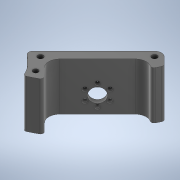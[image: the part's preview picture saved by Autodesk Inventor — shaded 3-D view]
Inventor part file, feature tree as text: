
AUTODESK INVENTOR PART (.ipt)
format: ipt  version: 2020 (Build 240168000, 168)  size: 688,128 bytes
history: native  units: mm
features: extrude x6, sketch x5, projected_geometry x2, other x1, chamfer x1, fillet x1
ambient origin geometry x8: Origin, YZ Plane, XZ Plane, XY Plane, X Axis, Y Axis, Z Axis, Center Point
bodies: Body1 (feature_tree)
feature tree (16):
  other  "Твердое тело1"
  sketch  "Эскиз1"
  extrude  "Выдавливание10"  Depth=4.0mm
  sketch  "Эскиз6"
  extrude  "Выдавливание13"  Depth=6.0mm
  extrude  "Выдавливание14"  Depth=35.0mm TaperAngle=0.0deg
  chamfer  "Фаска3"  Distance=59.0mm
  extrude  "Выдавливание15"  Depth=21.3mm
  fillet  "Сопряжение1"  Radius=15.0mm
  extrude  "Выдавливание16"  Depth=10.4mm
  extrude  "Выдавливание17"  Depth=2.5mm
  sketch  "Эскиз7"
  sketch  "Эскиз8"
  projected_geometry  "Спроецированная петля3"
  sketch  "Эскиз9"
  projected_geometry  "Спроецированная петля4"
